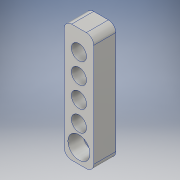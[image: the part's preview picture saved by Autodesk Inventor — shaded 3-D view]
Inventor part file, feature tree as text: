
AUTODESK INVENTOR PART (.ipt)
format: ipt  version: 2016 (Build 200138000, 138)  size: 147,968 bytes
history: native  units: in
note: dims shown in document units (in); Inventor stores cm internally (conversion verified against a paired STEP export)
features: sketch x5, extrude x2, hole x2, fillet x1, pattern_linear x1
ambient origin geometry x8: Origin, YZ Plane, XZ Plane, XY Plane, X Axis, Y Axis, Z Axis, Center Point
bodies: Body1 (feature_tree)
feature tree (11):
  extrude  "Stock Bar"  Depth=0.5in
  hole  "Motor Hole"  [1 undecoded]
  extrude  "Motor Hole Secondary"  Depth=0.25in
  sketch  "Sketch5"  dims[d14=0.25in]
  fillet  "Round Edges"  Radius=0.125in
  pattern_linear  "Mounting Holes"  Spacing1=0.25in  [1 undecoded]
  hole  "Hole2"  [1 undecoded]
  sketch  "Sketch1"  dims[d6=2.0in d7=0.5in]
  sketch  "Sketch4"  dims[d8=0.375in d9=0.0in d13=0.25in]
  sketch  "Sketch6"  dims[d15=0.257in d16=0.75in d17=0.375in d18=0.25in d19=0.5635in d20=1.0in d21=0.8108in d22=0.25in d24=0.125in]
  sketch  "Sketch7"  dims[d25=0.375in d26=0.25in d27=0.0in d28=0.257in d29=0.75in d30=0.375in d31=0.25in d32=0.5635in d33=1.0in d34=0.8108in d47=1.9685in d49=0.35in]
note: 3 required parameter values undecoded (feature->parameter linkage not recoverable at this tier; creation-order binding heuristic only, values carry confidence <= 0.55)
